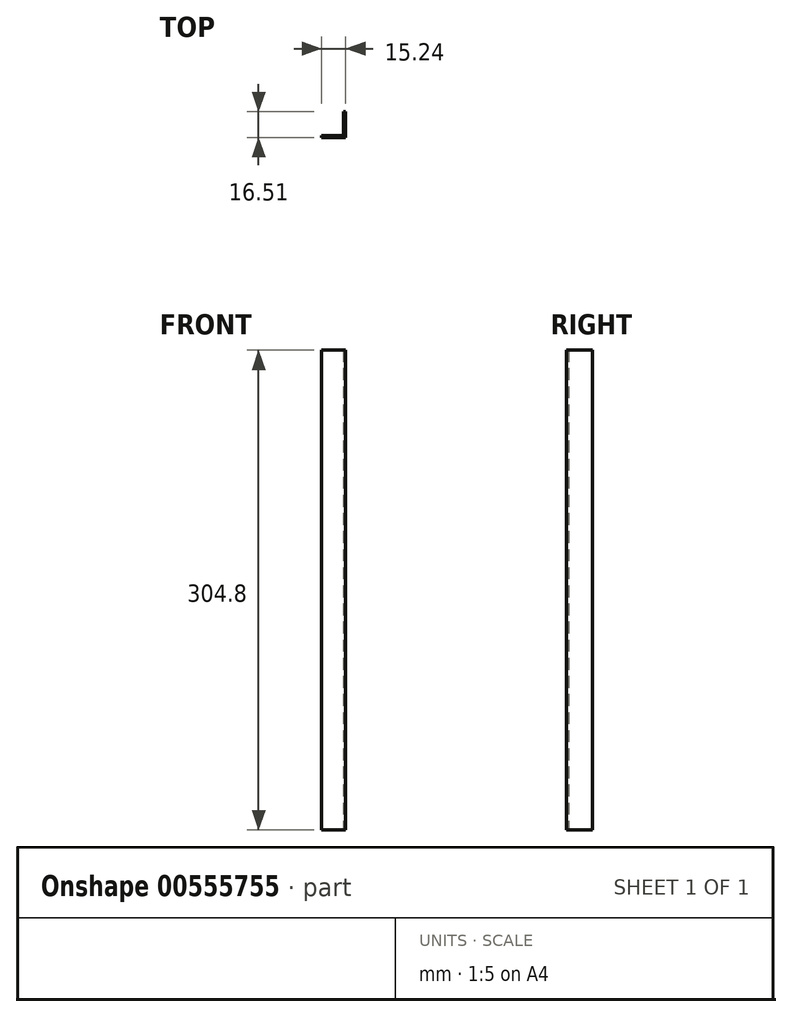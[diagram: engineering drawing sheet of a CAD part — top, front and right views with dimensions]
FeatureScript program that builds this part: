
annotation { "Feature Type Name" : "Feature", "Feature Type Description" : "" }
export const myFeature = defineFeature(function(context is Context, id is Id, definition is map)
    precondition{}
    {
        {
            var Q0;
            Q0=qCreatedBy(makeId("Top.planeOp"),FACE);
            var sketch = newSketch(context, id + "F0", { "sketchPlane" : qUnion([Q0])});
            skLineSegment(sketch, "E0.bottom", {"start": v(0, 0) * mm, "end": v(1.27, 0) * mm});
            skLineSegment(sketch, "E0.top", {"start": v(0, 15.24) * mm, "end": v(1.27, 15.24) * mm});
            skLineSegment(sketch, "E0.left", {"start": v(0, 0) * mm, "end": v(0, 15.24) * mm});
            skLineSegment(sketch, "E0.right", {"start": v(1.27, 0) * mm, "end": v(1.27, 15.24) * mm});
            skLineSegment(sketch, "E1.bottom", {"start": v(1.27, 0) * mm, "end": v(-13.97, 0) * mm});
            skLineSegment(sketch, "E1.top", {"start": v(1.27, -1.27) * mm, "end": v(-13.97, -1.27) * mm});
            skLineSegment(sketch, "E1.left", {"start": v(1.27, 0) * mm, "end": v(1.27, -1.27) * mm});
            skLineSegment(sketch, "E1.right", {"start": v(-13.97, 0) * mm, "end": v(-13.97, -1.27) * mm});
            skSolve(sketch);
        }
        {
            var Q0;
            Q0=makeQuery(id+"F0.imprint","IMPRINT",FACE,{"disambiguationData":[TD([[makeQuery(id+"F0.imprint","IMPRINT",EDGE,{"derivedFrom":sQuery(id+"F0.wireOp",EDGE,"E0.top")}),-1.0]])]});
            var Q1;
            Q1=makeQuery(id+"F0.imprint","IMPRINT",FACE,{"disambiguationData":[TD([[makeQuery(id+"F0.imprint","IMPRINT",EDGE,{"derivedFrom":sQuery(id+"F0.wireOp",EDGE,"E1.top")}),-1.0]])]});
            extrude(context, id + "F1", {"entities" : qUnion([Q0, Q1]), "depth" : 304.8 * mm, "offsetDistance" : 25.4 * mm});
        }
    });
